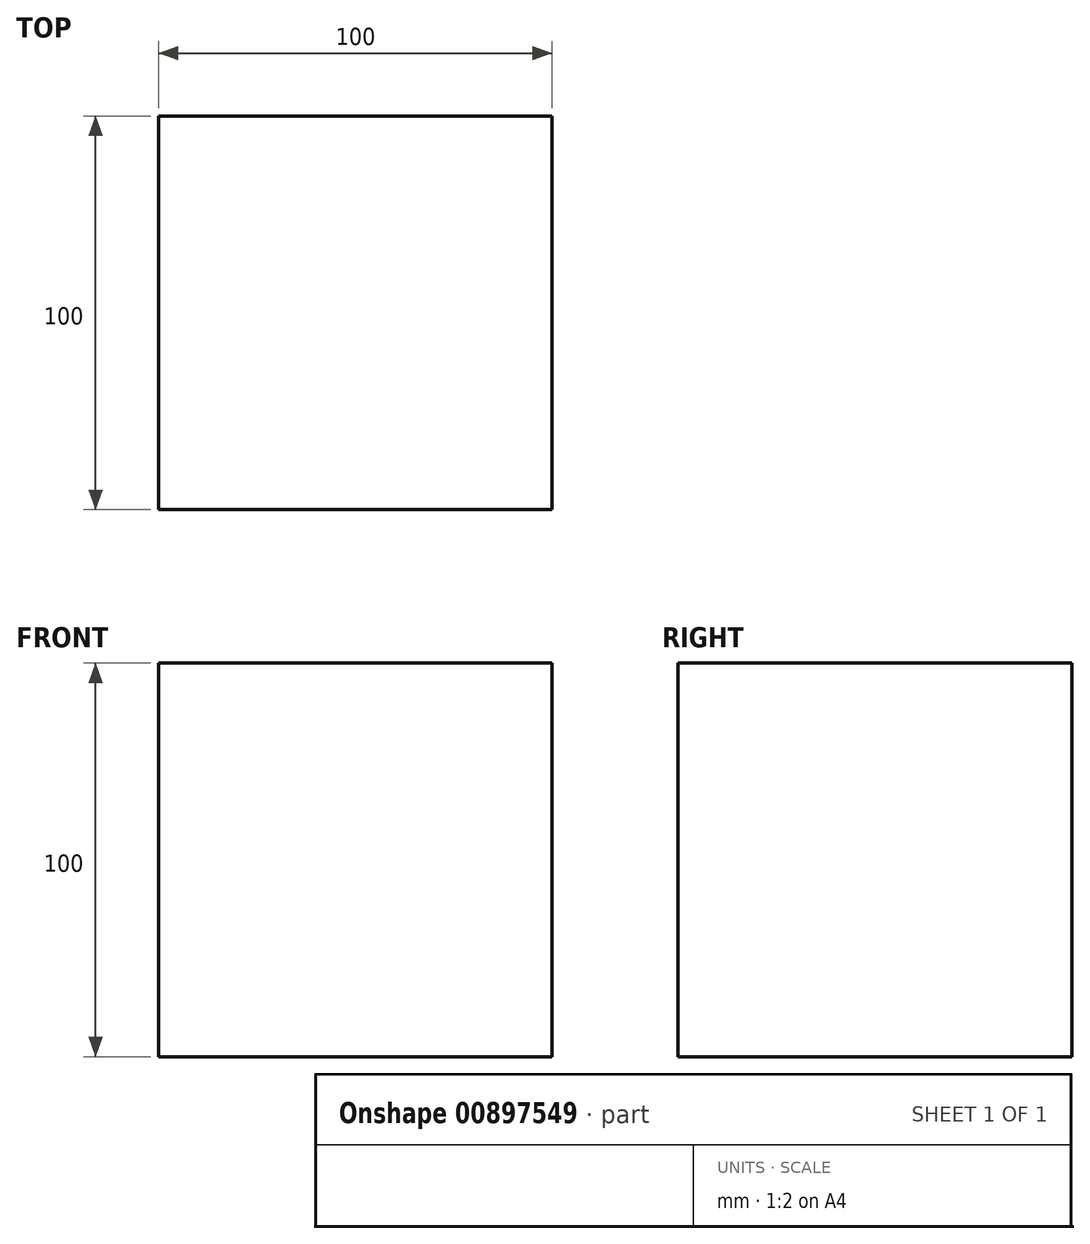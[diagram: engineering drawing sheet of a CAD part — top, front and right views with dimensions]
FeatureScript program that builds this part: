
annotation { "Feature Type Name" : "Feature", "Feature Type Description" : "" }
export const myFeature = defineFeature(function(context is Context, id is Id, definition is map)
    precondition{}
    {
        {
            var Q0;
            Q0=qCreatedBy(makeId("Top.planeOp"),FACE);
            var sketch = newSketch(context, id + "F0", { "sketchPlane" : qUnion([Q0])});
            skLineSegment(sketch, "E0.bottom", {"start": v(-83.42, 81.87) * mm, "end": v(16.58, 81.87) * mm});
            skLineSegment(sketch, "E0.top", {"start": v(-83.42, -18.13) * mm, "end": v(16.58, -18.13) * mm});
            skLineSegment(sketch, "E0.left", {"start": v(-83.42, 81.87) * mm, "end": v(-83.42, -18.13) * mm});
            skLineSegment(sketch, "E0.right", {"start": v(16.58, 81.87) * mm, "end": v(16.58, -18.13) * mm});
            skSolve(sketch);
        }
        {
            var Q0;
            Q0 = qSketchRegion(id + "F0", true);
            extrude(context, id + "F1", {"entities" : qUnion([Q0]), "depth" : 100 * mm, "offsetDistance" : 25 * mm});
        }
    });
